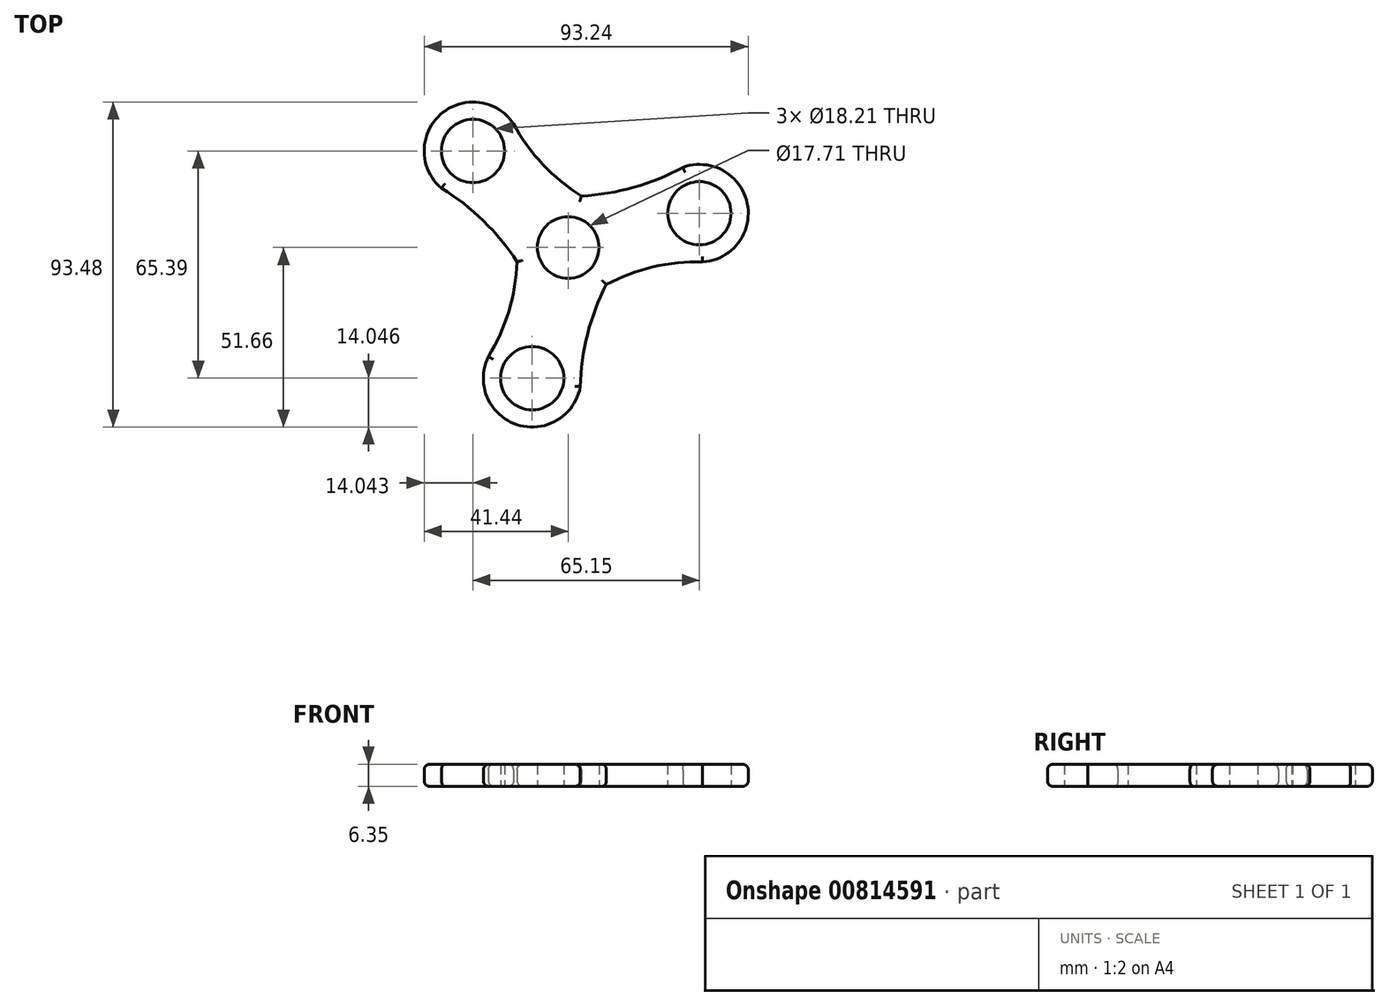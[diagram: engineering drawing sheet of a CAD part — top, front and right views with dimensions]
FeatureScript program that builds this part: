
annotation { "Feature Type Name" : "Feature", "Feature Type Description" : "" }
export const myFeature = defineFeature(function(context is Context, id is Id, definition is map)
    precondition{}
    {
        {
            var Q0;
            Q0=qCreatedBy(makeId("Top.planeOp"),FACE);
            var sketch = newSketch(context, id + "F0", { "sketchPlane" : qUnion([Q0])});
            skCircle(sketch, "E0", {"center": v(0, 0) * mm, "radius": 8.86 * mm});
            skCircle(sketch, "E1", {"center": v(-27.4, 27.78) * mm, "radius": 9.1 * mm});
            skArc(sketch, "E2", {"start": v(-14.67, 33.73) * mm, "mid": v(-37.28, 37.76) * mm, "end": v(-33.48, 15.11) * mm});
            skArc(sketch, "E3", {"start": v(-15.72, 35.58) * mm, "mid": v(-7.33, 23.93) * mm, "end": v(3.77, 14.82) * mm});
            skArc(sketch, "E4", {"start": v(-14.71, -4.15) * mm, "mid": v(-24.39, 7.67) * mm, "end": v(-36.45, 17.03) * mm});
            skCircle(sketch, "E5.1.0", {"center": v(-10.36, -37.61) * mm, "radius": 9.1 * mm});
            skArc(sketch, "E5.1.1", {"start": v(-21.88, -29.58) * mm, "mid": v(-14.06, -51.17) * mm, "end": v(3.65, -36.55) * mm});
            skArc(sketch, "E5.1.2", {"start": v(-22.96, -31.4) * mm, "mid": v(-17.06, -18.31) * mm, "end": v(-14.71, -4.15) * mm});
            skArc(sketch, "E5.1.3", {"start": v(10.95, -10.67) * mm, "mid": v(5.55, -24.95) * mm, "end": v(3.47, -40.08) * mm});
            skCircle(sketch, "E5.2.0", {"center": v(37.75, 9.84) * mm, "radius": 9.1 * mm});
            skArc(sketch, "E5.2.1", {"start": v(36.55, -4.16) * mm, "mid": v(51.34, 13.4) * mm, "end": v(29.83, 21.44) * mm});
            skArc(sketch, "E5.2.2", {"start": v(38.67, -4.18) * mm, "mid": v(24.39, -5.62) * mm, "end": v(10.95, -10.67) * mm});
            skArc(sketch, "E5.2.3", {"start": v(3.77, 14.82) * mm, "mid": v(18.83, 17.29) * mm, "end": v(32.98, 23.05) * mm});
            skSolve(sketch);
        }
        {
            var Q0;
            Q0=makeQuery(id+"F0.imprint","IMPRINT",FACE,{"disambiguationData":[TD([[makeQuery(id+"F0.imprint","IMPRINT",EDGE,{"derivedFrom":sQuery(id+"F0.wireOp",EDGE,"E0")}),-1.0]])]});
            extrude(context, id + "F1", {"entities" : qUnion([Q0]), "depth" : 6.35 * mm, "offsetDistance" : 25.4 * mm});
        }
        {
            var Q0;
            Q0=makeQuery(id+"F1.opExtrude","CAP_EDGE",EDGE,{"disambiguationData":[OSD([sQuery(id+"F0.wireOp",EDGE,"E5.2.2")])],"isStart":false});
            var Q1;
            Q1=makeQuery(id+"F1.opExtrude","CAP_EDGE",EDGE,{"disambiguationData":[OSD([sQuery(id+"F0.wireOp",EDGE,"E5.1.3")])],"isStart":false});
            var Q2;
            Q2=makeQuery(id+"F1.opExtrude","CAP_EDGE",EDGE,{"disambiguationData":[OSD([sQuery(id+"F0.wireOp",EDGE,"E5.1.2")])],"isStart":false});
            var Q3;
            Q3=makeQuery(id+"F1.opExtrude","CAP_EDGE",EDGE,{"disambiguationData":[OSD([sQuery(id+"F0.wireOp",EDGE,"E4")])],"isStart":false});
            var Q4;
            Q4=makeQuery(id+"F1.opExtrude","CAP_EDGE",EDGE,{"disambiguationData":[OSD([sQuery(id+"F0.wireOp",EDGE,"E3")])],"isStart":false});
            var Q5;
            Q5=makeQuery(id+"F1.opExtrude","CAP_EDGE",EDGE,{"disambiguationData":[OSD([sQuery(id+"F0.wireOp",EDGE,"E5.2.3")])],"isStart":false});
            var Q6;
            Q6=makeQuery(id+"F1.opExtrude","CAP_EDGE",EDGE,{"disambiguationData":[OSD([sQuery(id+"F0.wireOp",EDGE,"E5.2.1")])],"isStart":false});
            var Q7;
            Q7=makeQuery(id+"F1.opExtrude","CAP_EDGE",EDGE,{"disambiguationData":[OSD([sQuery(id+"F0.wireOp",EDGE,"E5.1.1")])],"isStart":false});
            var Q8;
            Q8=makeQuery(id+"F1.opExtrude","CAP_EDGE",EDGE,{"disambiguationData":[OSD([sQuery(id+"F0.wireOp",EDGE,"E2")])],"isStart":false});
            var Q9;
            Q9=makeQuery(id+"F1.opExtrude","CAP_EDGE",EDGE,{"disambiguationData":[OSD([sQuery(id+"F0.wireOp",EDGE,"E4")])],"isStart":true});
            var Q10;
            Q10=makeQuery(id+"F1.opExtrude","CAP_EDGE",EDGE,{"disambiguationData":[OSD([sQuery(id+"F0.wireOp",EDGE,"E2")])],"isStart":true});
            var Q11;
            Q11=makeQuery(id+"F1.opExtrude","CAP_EDGE",EDGE,{"disambiguationData":[OSD([sQuery(id+"F0.wireOp",EDGE,"E3")])],"isStart":true});
            var Q12;
            Q12=makeQuery(id+"F1.opExtrude","CAP_EDGE",EDGE,{"disambiguationData":[OSD([sQuery(id+"F0.wireOp",EDGE,"E5.1.3")])],"isStart":true});
            var Q13;
            Q13=makeQuery(id+"F1.opExtrude","CAP_EDGE",EDGE,{"disambiguationData":[OSD([sQuery(id+"F0.wireOp",EDGE,"E5.1.2")])],"isStart":true});
            var Q14;
            Q14=makeQuery(id+"F1.opExtrude","CAP_EDGE",EDGE,{"disambiguationData":[OSD([sQuery(id+"F0.wireOp",EDGE,"E5.2.2")])],"isStart":true});
            var Q15;
            Q15=makeQuery(id+"F1.opExtrude","CAP_EDGE",EDGE,{"disambiguationData":[OSD([sQuery(id+"F0.wireOp",EDGE,"E5.2.3")])],"isStart":true});
            var Q16;
            Q16=makeQuery(id+"F1.opExtrude","CAP_EDGE",EDGE,{"disambiguationData":[OSD([sQuery(id+"F0.wireOp",EDGE,"E5.2.1")])],"isStart":true});
            var Q17;
            Q17=makeQuery(id+"F1.opExtrude","CAP_EDGE",EDGE,{"disambiguationData":[OSD([sQuery(id+"F0.wireOp",EDGE,"E5.1.1")])],"isStart":true});
            fillet(context, id + "F2", {"entities" : qUnion([Q0, Q1, Q2, Q3, Q4, Q5, Q6, Q7, Q8, Q9, Q10, Q11, Q12, Q13, Q14, Q15, Q16, Q17]), "radius" : 1.59 * mm, "tangentPropagation" : true, "allowEdgeOverflow" : false});
        }
    });
